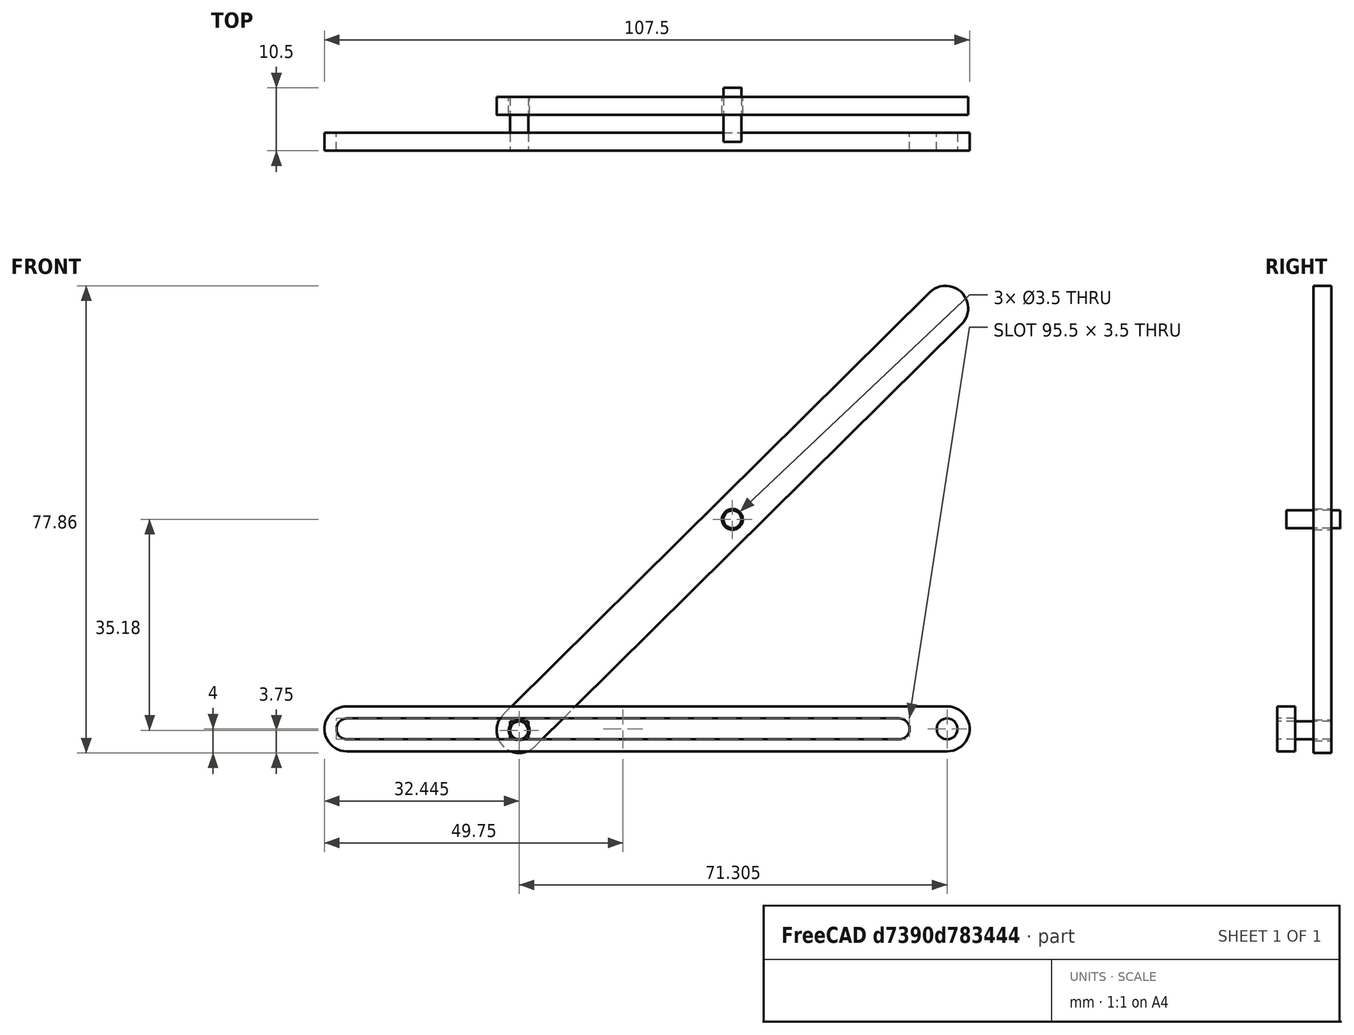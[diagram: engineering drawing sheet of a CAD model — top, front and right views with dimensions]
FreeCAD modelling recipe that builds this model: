
FCSTD DOCUMENT  (FreeCAD 1.0R39285 (Git))
Label: scissor_lift
License: All rights reserved
LicenseURL: https://en.wikipedia.org/wiki/All_rights_reserved
objects: App::FeaturePython×9, PartDesign::Body×7, Sketcher::SketchObject×4, PartDesign::Pad×4, PartDesign::FeatureBase×3, PartDesign::SubShapeBinder×2, Assembly::JointGroup×1, Assembly::AssemblyObject×1
note: 35 computed .brp shape members not serialized (recipe doc carries the construction recipe); baked Part::Feature solids carry a one-line shape summary decoded from their .brp

FEATURE [Sketcher::SketchObject] Sketch
  ArcFitTolerance = 1e-06
  AttachmentSupport = -> [XY_Plane]
  FullyConstrained = true
  MakeInternals = false
  MapMode = 5
  sketch-geometry (9):
    g0: ArcOfCircle CenterX=-50 CenterY=2e-16 CenterZ=0 NormalX=0 NormalY=0 NormalZ=1 AngleXU=0 Radius=3.75 StartAngle=1.5708 EndAngle=4.71239
    g1: ArcOfCircle CenterX=50 CenterY=-2e-16 CenterZ=0 NormalX=0 NormalY=0 NormalZ=1 AngleXU=0 Radius=3.75 StartAngle=4.71239 EndAngle=7.85398
    g2: LineSegment StartX=-50 StartY=3.75 StartZ=0 EndX=50 EndY=3.75 EndZ=0
    g3: LineSegment StartX=-50 StartY=-3.75 StartZ=0 EndX=50 EndY=-3.75 EndZ=0
    g4: ArcOfCircle CenterX=-50 CenterY=2e-16 CenterZ=0 NormalX=0 NormalY=0 NormalZ=1 AngleXU=0 Radius=1.75 StartAngle=1.5708 EndAngle=4.71239
    g5: ArcOfCircle CenterX=42 CenterY=3e-16 CenterZ=0 NormalX=0 NormalY=0 NormalZ=1 AngleXU=0 Radius=1.75 StartAngle=4.71239 EndAngle=7.85398
    g6: LineSegment StartX=-50 StartY=1.75 StartZ=0 EndX=42 EndY=1.75 EndZ=0
    g7: LineSegment StartX=-50 StartY=-1.75 StartZ=0 EndX=42 EndY=-1.75 EndZ=0
    g8: Circle CenterX=50 CenterY=-2e-16 CenterZ=0 NormalX=0 NormalY=0 NormalZ=1 AngleXU=0 Radius=1.75
  constraints (20):
    c: Tangent(g0,g2) = 1.5708
    c: Tangent(g0,g3) = -1.5708
    c: Tangent(g1,g2) = 1.5708
    c: Tangent(g1,g3) = -1.5708
    c: Equal(g0,g1)
    c: Horizontal(g3)
    c: Symmetric(g0,g1,g-1)
    c: DistanceX(g0,g1) = 100
    c: DistanceY(g0,g0) = 7.5
    c: Tangent(g4,g6) = 1.5708
    c: Tangent(g4,g7) = -1.5708
    c: Tangent(g5,g6) = 1.5708
    c: Tangent(g5,g7) = -1.5708
    c: Equal(g4,g5)
    c: Horizontal(g7)
    c: Distance(g4,g4) = 3.5
    c: Coincident(g8,g1)
    c: Diameter(g8) = 3.5
    c: DistanceX(g5,g1) = 8
    c: Coincident(g4,g0)
FEATURE [PartDesign::Pad] Pad
  Direction = (0,0,1)
  Length = 3
  Length2 = 10
  Profile = -> Sketch
  ReferenceAxis = -> Sketch [N_Axis]
  Refine = true
  Suppressed = false
  Type = 0
FEATURE [PartDesign::Body] Body  label="base"
  AllowCompound = false
  Group = -> [Sketch,Pad]
  Origin = -> Origin
  Placement = pos=(0,1.5,1.5) rot=(1,0,0;1.5708rad)
  Tip = -> Pad
FEATURE [PartDesign::SubShapeBinder] Binder
  BindCopyOnChange = 0
  BindMode = 0
  ClaimChildren = false
  Context = -> Assembly [Body001.Binder.]
  Fuse = false
  MakeFace = true
  OffsetFill = false
  OffsetIntersection = false
  OffsetJoinType = 0
  OffsetOpenResult = false
  PartialLoad = false
  Refine = true
  Relative = true
  Support = -> [Body]
  _Version = 2
FEATURE [Sketcher::SketchObject] Sketch001
  ArcFitTolerance = 1e-06
  AttachmentSupport = -> [XY_Plane001]
  ExternalGeometry = -> [Binder]
  FullyConstrained = true
  MakeInternals = false
  MapMode = 5
  sketch-geometry (6):
    g0: ArcOfCircle CenterX=-50 CenterY=1e-16 CenterZ=0 NormalX=0 NormalY=0 NormalZ=1 AngleXU=0 Radius=3.75 StartAngle=1.5708 EndAngle=4.71239
    g1: ArcOfCircle CenterX=50 CenterY=-1e-16 CenterZ=0 NormalX=0 NormalY=0 NormalZ=1 AngleXU=0 Radius=3.75 StartAngle=4.71239 EndAngle=7.85398
    g2: LineSegment StartX=-50 StartY=3.75 StartZ=0 EndX=50 EndY=3.75 EndZ=0
    g3: LineSegment StartX=-50 StartY=-3.75 StartZ=0 EndX=50 EndY=-3.75 EndZ=0
    g4: Circle CenterX=-50 CenterY=1e-16 CenterZ=0 NormalX=0 NormalY=0 NormalZ=1 AngleXU=0 Radius=1.75
    g5: Circle CenterX=0 CenterY=0 CenterZ=0 NormalX=0 NormalY=0 NormalZ=1 AngleXU=0 Radius=1.75
  constraints (13):
    c: Tangent(g0,g2) = 1.5708
    c: Tangent(g0,g3) = -1.5708
    c: Tangent(g1,g2) = 1.5708
    c: Tangent(g1,g3) = -1.5708
    c: Equal(g0,g1)
    c: Horizontal(g2)
    c: Symmetric(g0,g1,g-1)
    c: Equal(g2,g-3)
    c: Equal(g1,g-4)
    c: Coincident(g4,g0)
    c: Equal(g4,g-5)
    c: Coincident(g5,g-1)
    c: Equal(g5,g-5)
FEATURE [PartDesign::Pad] Pad001
  Direction = (0,0,1)
  Length = 3
  Length2 = 10
  Profile = -> Sketch001
  ReferenceAxis = -> Sketch001 [N_Axis]
  Refine = true
  Suppressed = false
  Type = 0
FEATURE [PartDesign::Body] Body001  label="arm_1"
  AllowCompound = false
  Group = -> [Binder,Sketch001,Pad001]
  Origin = -> Origin001
  Placement = pos=(14.2248,1.49999,36.4304) rot=(0.276713,0.679496,0.679496;3.68151rad)
  Tip = -> Pad001
FEATURE [PartDesign::FeatureBase] Clone
  BaseFeature = -> Body001
  Placement = pos=(0,14,0) rot=(0,0,1;0rad)
  Suppressed = false
FEATURE [PartDesign::Body] Body002  label="arm_2"
  AllowCompound = false
  Group = -> [Clone]
  Origin = -> Origin002
  Placement = pos=(24.0753,7.5,26.4822) rot=(0.864392,-0.355546,0.355546;1.71601rad)
  Tip = -> Clone
FEATURE [Sketcher::SketchObject] Sketch002
  ArcFitTolerance = 1e-06
  AttachmentSupport = -> [XY_Plane003]
  FullyConstrained = true
  MakeInternals = false
  MapMode = 5
  sketch-geometry (1):
    g0: Circle CenterX=0 CenterY=0 CenterZ=0 NormalX=0 NormalY=0 NormalZ=1 AngleXU=0 Radius=1.5
  constraints (2):
    c: Coincident(g0,g-1)
    c: Diameter(g0) = 3
FEATURE [PartDesign::Pad] Pad002
  Direction = (0,0,1)
  Length = 9
  Length2 = 10
  Profile = -> Sketch002
  ReferenceAxis = -> Sketch002 [N_Axis]
  Refine = true
  Suppressed = false
  Type = 0
FEATURE [PartDesign::Body] Body003  label="pin_1"
  AllowCompound = false
  Group = -> [Sketch002,Pad002]
  Origin = -> Origin003
  Placement = pos=(50,7.5,1.5) rot=(0.772485,0.449036,-0.449036;1.82612rad)
  Tip = -> Pad002
FEATURE [PartDesign::FeatureBase] Clone001
  BaseFeature = -> Body003
  Placement = pos=(-65,0,0) rot=(0,0,1;0rad)
  Suppressed = false
FEATURE [PartDesign::Body] Body004  label="pin_2"
  AllowCompound = false
  Group = -> [Clone001]
  Origin = -> Origin004
  Placement = pos=(58.3467,2.05569e-06,-11.3007) rot=(-0.850439,0.371991,0.371991;1.73209rad)
  Tip = -> Clone001
FEATURE [PartDesign::FeatureBase] Clone002
  BaseFeature = -> Body003
  Placement = pos=(-65,0,0) rot=(0,0,1;0rad)
  Suppressed = false
FEATURE [PartDesign::Body] Body005  label="pin_3"
  AllowCompound = false
  Group = -> [Clone002]
  Origin = -> Origin005
  Placement = pos=(15.1366,-1.50001,55.0741) rot=(-0.799856,-0.424399,-0.424399;1.79229rad)
  Tip = -> Clone002
FEATURE [App::FeaturePython] GroundedJoint  # Assembly grounded joint (typed FeaturePython)
  ObjectToGround = -> Body
  Placement = pos=(0,1.5,1.5) rot=(1,0,0;1.5708rad)
FEATURE [App::FeaturePython] Joint  label="Revolute"  # Assembly joint (typed FeaturePython)
  Activated = true
  AngleMax = 0
  AngleMin = 0
  Detach1 = false
  Detach2 = false
  Distance = 0
  Distance2 = 0
  EnableAngleMax = false
  EnableAngleMin = false
  EnableLengthMax = false
  EnableLengthMin = false
  JointType = 1 (Revolute)
  LengthMax = 0
  LengthMin = 0
  Placement1 = pos=(0,-7.1e-15,9) rot=(0,0,1;0rad)
  Placement2 = pos=(50,-2e-16,3) rot=(0,0,1;0rad)
  Reference1 = -> Assembly [Body003.Face1,Body003.Edge3]
  Reference2 = -> Assembly [Body.Edge27,Body.Edge27]
FEATURE [App::FeaturePython] Joint001  label="Cylindrical"  # Assembly joint (typed FeaturePython)
  Activated = true
  AngleMax = 0
  AngleMin = 0
  Detach1 = false
  Detach2 = false
  Distance = 0
  Distance2 = 0
  EnableAngleMax = false
  EnableAngleMin = false
  EnableLengthMax = false
  EnableLengthMin = false
  JointType = 2 (Cylindrical)
  LengthMax = 0
  LengthMin = 0
  Placement1 = pos=(3.6e-15,0,4.5) rot=(0,0,1;0rad)
  Placement2 = pos=(-50,2.13e-14,1.5) rot=(0,0,1;0rad)
  Reference1 = -> Assembly [Body003.Face1,Body003.Face1]
  Reference2 = -> Assembly [Body001.Face6,Body001.Face6]
FEATURE [App::FeaturePython] Joint002  label="Distance"  # Assembly joint (typed FeaturePython)
  Activated = true
  AngleMax = 0
  AngleMin = 0
  Detach1 = false
  Detach2 = false
  Distance = 0
  Distance2 = 0
  EnableAngleMax = false
  EnableAngleMin = false
  EnableLengthMax = false
  EnableLengthMin = false
  JointType = 5 (Distance)
  LengthMax = 0
  LengthMin = 0
  Placement1 = pos=(0.620769,0,-2e-16) rot=(0,0,1;0rad)
  Placement2 = pos=(1.86655,-7e-16,0) rot=(0,0,1;0rad)
  Reference1 = -> Assembly [Body001.Face7,Body001.Vertex11]
  Reference2 = -> Assembly [Body.Face10,Body.Vertex7]
FEATURE [App::FeaturePython] Joint003  label="Revolute001"  # Assembly joint (typed FeaturePython)
  Activated = true
  AngleMax = 0
  AngleMin = 0
  Detach1 = false
  Detach2 = false
  Distance = 0
  Distance2 = 0
  EnableAngleMax = false
  EnableAngleMin = false
  EnableLengthMax = false
  EnableLengthMin = false
  JointType = 1 (Revolute)
  LengthMax = 0
  LengthMin = 0
  Placement1 = pos=(-65,-1.42e-14,4.5) rot=(0,0,1;0rad)
  Placement2 = pos=(3.6e-15,0,3) rot=(0,0,1;0rad)
  Reference1 = -> Assembly [Body004.Face1,Body004.Face1]
  Reference2 = -> Assembly [Body001.Edge15,Body001.Edge15]
FEATURE [App::FeaturePython] Joint004  label="Revolute002"  # Assembly joint (typed FeaturePython)
  Activated = true
  AngleMax = 0
  AngleMin = 0
  Detach1 = false
  Detach2 = false
  Distance = 0
  Distance2 = 0
  EnableAngleMax = false
  EnableAngleMin = false
  EnableLengthMax = false
  EnableLengthMin = false
  JointType = 1 (Revolute)
  LengthMax = 0
  LengthMin = 0
  Placement1 = pos=(0,14,3) rot=(0,0,1;0rad)
  Placement2 = pos=(-65,-1.42e-14,4.5) rot=(0,0,1;0rad)
  Reference1 = -> Assembly [Body002.Edge15,Body002.Edge15]
  Reference2 = -> Assembly [Body004.Face1,Body004.Face1]
FEATURE [App::FeaturePython] Joint005  label="Revolute003"  # Assembly joint (typed FeaturePython)
  Activated = true
  AngleMax = 0
  AngleMin = 0
  Detach1 = false
  Detach2 = false
  Distance = 0
  Distance2 = 0
  EnableAngleMax = false
  EnableAngleMin = false
  EnableLengthMax = false
  EnableLengthMin = false
  JointType = 1 (Revolute)
  LengthMax = 0
  LengthMin = 0
  Placement1 = pos=(-65,-3.6e-15,9) rot=(0,0,1;0rad)
  Placement2 = pos=(-50,14,1.8e-15) rot=(0,0,1;0rad)
  Reference1 = -> Assembly [Body005.Face3,Body005.Face3]
  Reference2 = -> Assembly [Body002.Edge17,Body002.Edge17]
FEATURE [PartDesign::SubShapeBinder] Binder001
  BindCopyOnChange = 0
  BindMode = 0
  ClaimChildren = false
  Context = -> Assembly [Body006.Binder001.]
  Fuse = false
  MakeFace = true
  OffsetFill = false
  OffsetIntersection = false
  OffsetJoinType = 0
  OffsetOpenResult = false
  PartialLoad = false
  Refine = true
  Relative = true
  Support = -> [Body005]
  _Version = 2
FEATURE [Sketcher::SketchObject] Sketch003
  ArcFitTolerance = 1e-06
  AttachmentSupport = -> [XZ_Plane007]
  ExternalGeometry = -> [Binder001]
  FullyConstrained = false
  MakeInternals = false
  MapMode = 5
  Placement = pos=(0,0,0) rot=(1,0,0;1.5708rad)
  sketch-geometry (4):
    g0: LineSegment StartX=-36.1694 StartY=2.99185 StartZ=0 EndX=-36.1694 EndY=-0.00815282 EndZ=0
    g1: LineSegment StartX=-36.1694 StartY=-0.00815282 StartZ=0 EndX=-33.1694 EndY=-0.00815282 EndZ=0
    g2: LineSegment StartX=-33.1694 StartY=-0.00815282 StartZ=0 EndX=-33.1694 EndY=2.99185 EndZ=0
    g3: LineSegment StartX=-33.1694 StartY=2.99185 StartZ=0 EndX=-36.1694 EndY=2.99185 EndZ=0
  constraints (10):
    c: Coincident(g0,g1)
    c: Coincident(g1,g2)
    c: Coincident(g2,g3)
    c: Coincident(g3,g0)
    c: Vertical(g0)
    c: Vertical(g2)
    c: Horizontal(g1)
    c: Horizontal(g3)
    c: Equal(g3,g2)
    c: DistanceX(g3,g3) = 3
FEATURE [PartDesign::Pad] Pad003
  Direction = (0,-1,2e-16)
  Length = 3
  Length2 = 10
  Placement = pos=(0,0,0) rot=(1,0,0;1.5708rad)
  Profile = -> Sketch003
  ReferenceAxis = -> Sketch003 [N_Axis]
  Refine = true
  Suppressed = false
  Type = 0
FEATURE [PartDesign::Body] Body006  label="constraint"
  AllowCompound = false
  Group = -> [Sketch003,Binder001,Pad003]
  Origin = -> Origin007
  Placement = pos=(13.3648,1.5,-0.241847) rot=(0.99808,0,0;0rad)
  Tip = -> Pad003
FEATURE [App::FeaturePython] Joint006  label="Revolute004"  # Assembly joint (typed FeaturePython)
  Activated = true
  AngleMax = 0
  AngleMin = 0
  Detach1 = false
  Detach2 = false
  Distance = 0
  Distance2 = 0
  EnableAngleMax = false
  EnableAngleMin = false
  EnableLengthMax = false
  EnableLengthMin = false
  JointType = 1 (Revolute)
  LengthMax = 0
  LengthMin = 0
  Placement1 = pos=(-34.6694,-3,1.49185) rot=(-0.576242,-0.576242,-0.576242;2.0944rad)
  Placement2 = pos=(-65,-3.6e-15,-1.6e-15) rot=(0,0,1;0rad)
  Reference1 = -> Assembly [Body006.Face6,Body006.Face6]
  Reference2 = -> Assembly [Body005.Face2,Body005.Face2]
FEATURE [App::FeaturePython] Joint007  label="Slider"  # Assembly joint (typed FeaturePython)
  Activated = true
  AngleMax = 0
  AngleMin = 0
  Detach1 = false
  Detach2 = false
  Distance = 0
  Distance2 = 0
  EnableAngleMax = false
  EnableAngleMin = false
  EnableLengthMax = true
  EnableLengthMin = true
  JointType = 3 (Slider)
  LengthMax = -0.5
  LengthMin = -92.25
  Offset2 = pos=(0,0,0) rot=(0,0,-1;0.10472rad)
  Placement1 = pos=(-34.6694,-3,-0.00815282) rot=(0.707107,0,0.707107;3.14159rad)
  Placement2 = pos=(-50,-1.75,3) rot=(0.706622,0.037032,0.706622;3.06756rad)
  Reference1 = -> Assembly [Body006.Edge7,Body006.Edge7]
  Reference2 = -> Assembly [Body.Edge19,Body.Vertex12]
FEATURE [Assembly::JointGroup] Joints
  Group = -> [GroundedJoint,Joint,Joint001,Joint002,Joint003,Joint004,Joint005,Joint006,Joint007]
FEATURE [Assembly::AssemblyObject] Assembly
  Group = -> [Joints,Body,Body001,Body002,Body003,Body004,Body005,GroundedJoint,Joint,Joint001,Joint002,Joint003,Joint004,Joint005,Body006,Joint006,Joint007]
  Origin = -> Origin006
  Type = Assembly
